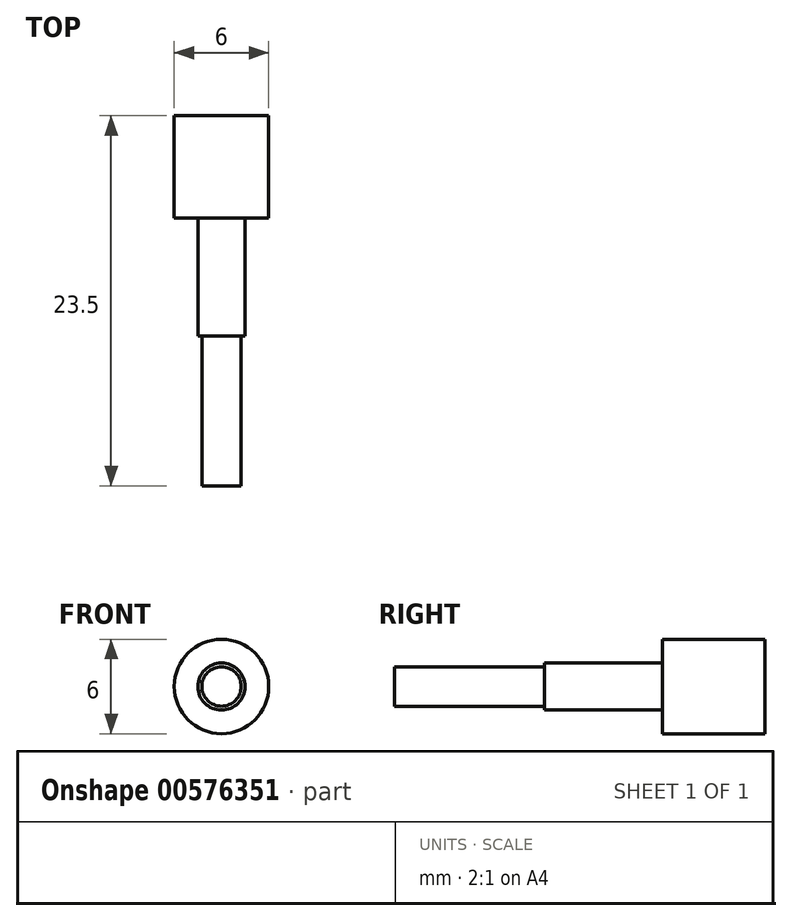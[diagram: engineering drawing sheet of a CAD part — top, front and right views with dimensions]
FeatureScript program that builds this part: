
annotation { "Feature Type Name" : "Feature", "Feature Type Description" : "" }
export const myFeature = defineFeature(function(context is Context, id is Id, definition is map)
    precondition{}
    {
        {
            var Q0;
            Q0=qCreatedBy(makeId("Top.planeOp"),FACE);
            var sketch = newSketch(context, id + "F0", { "sketchPlane" : qUnion([Q0])});
            skLineSegment(sketch, "E0", {"start": v(0, 15.04) * mm, "end": v(0, -10.82) * mm, "construction": true});
            skLineSegment(sketch, "E1", {"start": v(0, 14) * mm, "end": v(-3, 14) * mm});
            skLineSegment(sketch, "E2", {"start": v(-3, 14) * mm, "end": v(-3, 7.5) * mm});
            skLineSegment(sketch, "E3", {"start": v(-3, 7.5) * mm, "end": v(-1.5, 7.5) * mm});
            skLineSegment(sketch, "E4", {"start": v(-1.5, 7.5) * mm, "end": v(-1.5, 0) * mm});
            skLineSegment(sketch, "E5", {"start": v(-1.5, 0) * mm, "end": v(-1.25, 0) * mm});
            skLineSegment(sketch, "E6", {"start": v(-1.25, 0) * mm, "end": v(-1.25, -9.5) * mm});
            skLineSegment(sketch, "E7", {"start": v(-1.25, -9.5) * mm, "end": v(0, -9.5) * mm});
            skLineSegment(sketch, "E8", {"start": v(0, -9.5) * mm, "end": v(0, 14) * mm});
            skSolve(sketch);
        }
        {
            var Q0;
            Q0 = qSketchRegion(id + "F0", true);
            var Q1;
            Q1=sQuery(id+"F0.wireOp",EDGE,"E0");
            revolve(context, id + "F1", {"surfaceOperationType" : NewSurfaceOperationType.NEW, "entities" : qUnion([Q0]), "axis" : qUnion([Q1]), "revolveType" : RevolveType.FULL});
        }
    });
